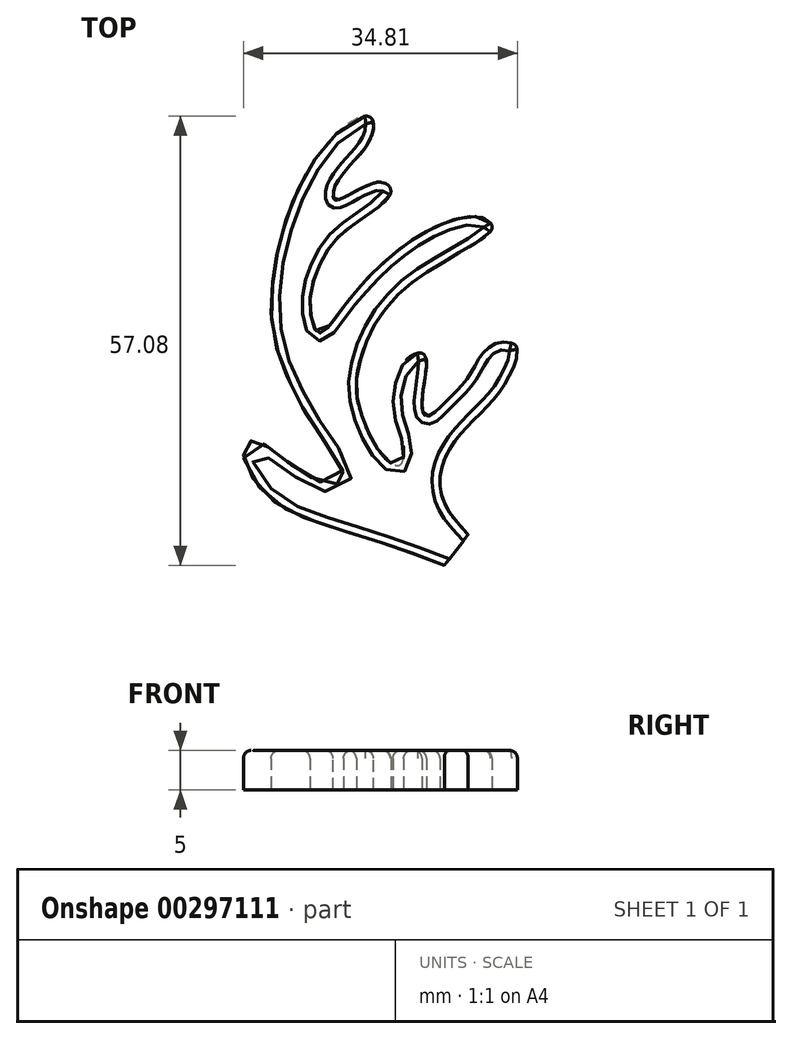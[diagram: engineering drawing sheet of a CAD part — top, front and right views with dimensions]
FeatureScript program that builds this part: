
annotation { "Feature Type Name" : "Feature", "Feature Type Description" : "" }
export const myFeature = defineFeature(function(context is Context, id is Id, definition is map)
    precondition{}
    {
        {
            var Q0;
            Q0=qCreatedBy(makeId("Top.planeOp"),FACE);
            var sketch = newSketch(context, id + "F0", { "sketchPlane" : qUnion([Q0])});
            skFitSpline(sketch, "E0", {"points": [v(-21.64, -15.5) * mm, v(-24.69, -11.4) * mm, v(-24.94, -6.8) * mm, v(-22.43, -2.53) * mm, v(-19.96, 0) * mm, v(-17.54, 2.73) * mm, v(-15.95, 5.62) * mm, v(-15.4, 7.25) * mm, v(-15.62, 8.54) * mm, v(-16.58, 8.88) * mm, v(-17.88, 8.88) * mm, v(-19.8, 7.5) * mm, v(-21.47, 4.7) * mm, v(-24.27, 1.56) * mm, v(-25.9, 0) * mm, v(-26.74, -0.49) * mm, v(-27.36, 0) * mm, v(-27.2, 3.94) * mm, v(-26.99, 6.83) * mm, v(-27.57, 7.54) * mm, v(-29.41, 6.75) * mm, v(-30.75, 4.07) * mm, v(-31.13, 2.52) * mm, v(-31, -0.4) * mm, v(-29.91, -4.04) * mm, v(-30.04, -6.3) * mm, v(-30.67, -6.8) * mm, v(-33.05, -4.75) * mm, v(-35.26, 0) * mm, v(-35.8, 2.65) * mm, v(-35.51, 6.04) * mm, v(-34.05, 10.05) * mm, v(-32.63, 12.51) * mm, v(-30.29, 15.23) * mm, v(-27.82, 17.2) * mm, v(-22.14, 20.66) * mm, v(-19.84, 22.09) * mm, v(-18.63, 23.34) * mm, v(-19.09, 24.43) * mm, v(-21.39, 24.89) * mm, v(-26.99, 22.96) * mm, v(-33.42, 18.03) * mm, v(-37.4, 13.52) * mm, v(-39.48, 10.76) * mm, v(-40.57, 10.09) * mm, v(-41.37, 11.18) * mm, v(-41.53, 15.73) * mm, v(-39.4, 20.75) * mm, v(-37.52, 22.84) * mm, v(-34, 25.39) * mm, v(-32.13, 26.9) * mm, v(-31.46, 27.9) * mm, v(-31.7, 28.89) * mm], "startDerivative": vector(-142.07, 152.37) * mm, "endDerivative": vector(-89.78, 104.48) * mm});
            skFitSpline(sketch, "E1", {"points": [v(-31.7, 28.89) * mm, v(-32.53, 29.2) * mm, v(-33.4, 29.2) * mm, v(-36.29, 27.92) * mm, v(-37.91, 27.07) * mm, v(-38.64, 27.05) * mm, v(-38.64, 28.49) * mm, v(-37.57, 30.24) * mm, v(-36.44, 31.65) * mm, v(-35.17, 33.03) * mm, v(-34.05, 34.8) * mm, v(-33.64, 36.44) * mm, v(-34.13, 37.55) * mm, v(-36.44, 36.94) * mm, v(-40.2, 33.4) * mm, v(-42.22, 30.26) * mm, v(-44.05, 26.47) * mm, v(-45.13, 23.15) * mm, v(-45.95, 20.01) * mm, v(-46.42, 16.93) * mm, v(-46.65, 12.75) * mm, v(-45.78, 7.6) * mm, v(-44.35, 4) * mm, v(-41.49, -1.38) * mm, v(-37.76, -7) * mm, v(-37.52, -8.5) * mm, v(-38.02, -9.04) * mm, v(-40.53, -8.76) * mm, v(-43.93, -6.74) * mm, v(-46.16, -5.15) * mm, v(-47.9, -3.77) * mm, v(-49.15, -3.58) * mm, v(-49.9, -4.18) * mm, v(-50.17, -5.63) * mm, v(-48.96, -8.4) * mm, v(-45.96, -11.58) * mm, v(-41.36, -13.75) * mm, v(-33.58, -16.23) * mm, v(-29.45, -17.63) * mm, v(-24.66, -19.43) * mm], "startDerivative": vector(-59.32, 25.1) * mm, "endDerivative": vector(144.03, -54.95) * mm});
            skLineSegment(sketch, "E2", {"start": v(-24.66, -19.43) * mm, "end": v(-21.64, -15.5) * mm});
            skSolve(sketch);
        }
        {
            var Q0;
            Q0=makeQuery(id+"F0.imprint","IMPRINT",FACE,{"disambiguationData":[TD([[makeQuery(id+"F0.imprint","IMPRINT",EDGE,{"derivedFrom":sQuery(id+"F0.wireOp",EDGE,"E0")}),1.0]])]});
            extrude(context, id + "F1", {"entities" : qUnion([Q0]), "depth" : 5 * mm});
        }
        {
            var Q0;
            Q0=makeQuery(id+"F1.opExtrude","CAP_EDGE",EDGE,{"disambiguationData":[OSD([sQuery(id+"F0.wireOp",EDGE,"E0")])],"isStart":false});
            fillet(context, id + "F2", {"entities" : qUnion([Q0]), "radius" : 1 * mm, "tangentPropagation" : true, "allowEdgeOverflow" : false});
        }
        {
            var Q0;
            Q0=makeQuery(id+"F1.opExtrude","CAP_EDGE",EDGE,{"disambiguationData":[OSD([sQuery(id+"F0.wireOp",EDGE,"E1")])],"isStart":false});
            fillet(context, id + "F3", {"entities" : qUnion([Q0]), "radius" : 1 * mm, "tangentPropagation" : true, "allowEdgeOverflow" : false});
        }
    });
